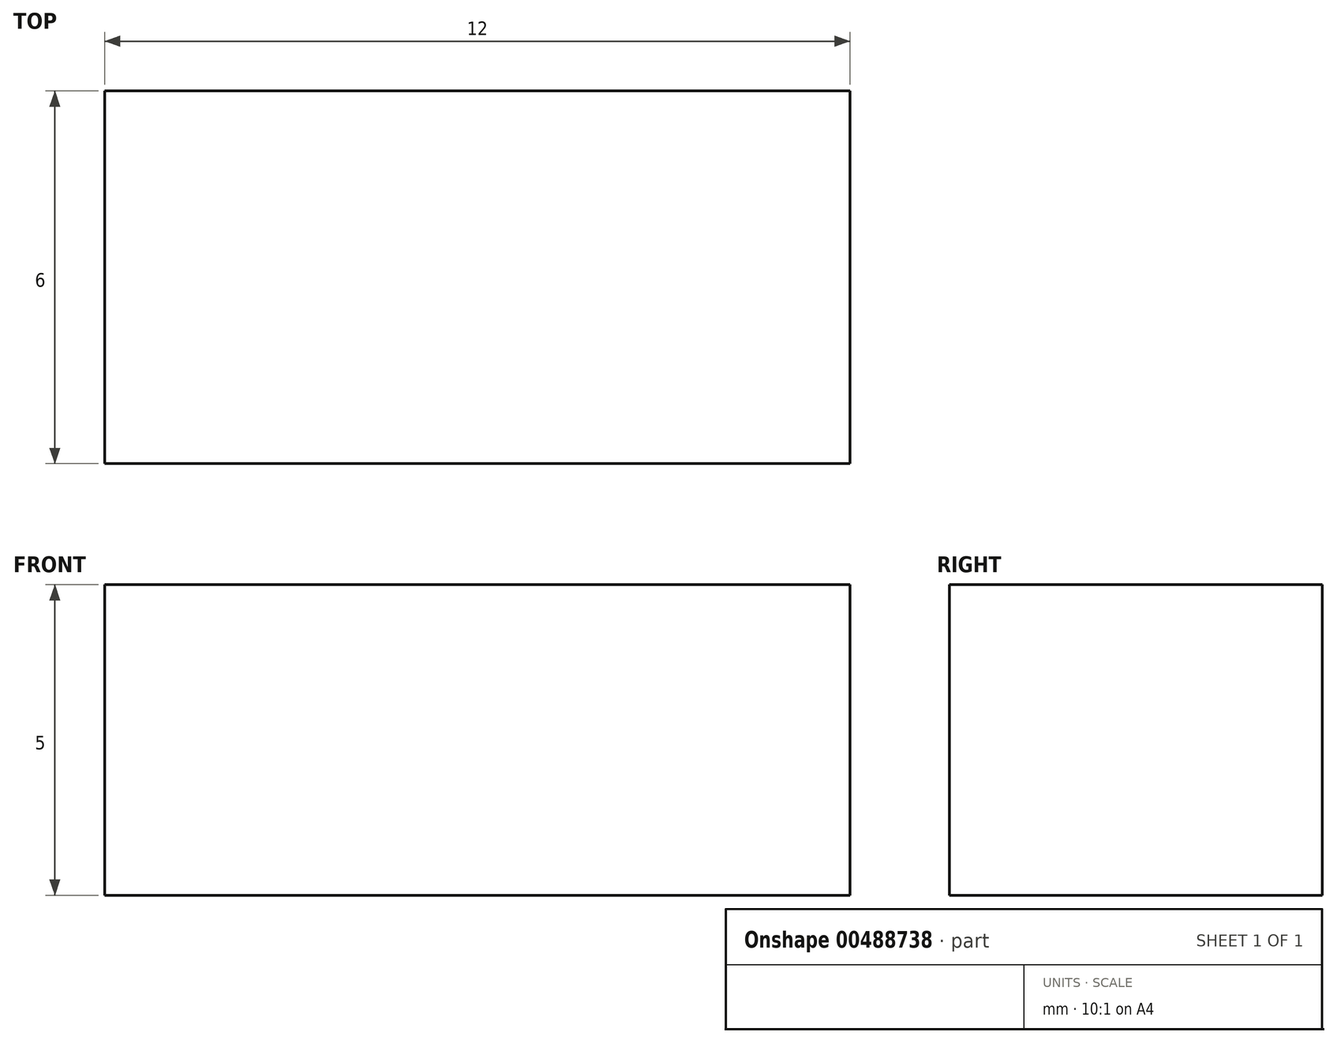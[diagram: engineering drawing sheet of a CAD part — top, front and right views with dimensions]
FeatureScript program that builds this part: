
annotation { "Feature Type Name" : "Feature", "Feature Type Description" : "" }
export const myFeature = defineFeature(function(context is Context, id is Id, definition is map)
    precondition{}
    {
        {
            var Q0;
            Q0=qCreatedBy(makeId("Top.planeOp"),FACE);
            var sketch = newSketch(context, id + "F0", { "sketchPlane" : qUnion([Q0])});
            skLineSegment(sketch, "E0.bottom", {"start": v(0, 0) * mm, "end": v(12, 0) * mm});
            skLineSegment(sketch, "E0.top", {"start": v(0, 6) * mm, "end": v(12, 6) * mm});
            skLineSegment(sketch, "E0.left", {"start": v(0, 0) * mm, "end": v(0, 6) * mm});
            skLineSegment(sketch, "E0.right", {"start": v(12, 0) * mm, "end": v(12, 6) * mm});
            skSolve(sketch);
        }
        {
            var Q0;
            Q0=makeQuery(id+"F0.imprint","IMPRINT",FACE,{"disambiguationData":[TD([[makeQuery(id+"F0.imprint","IMPRINT",EDGE,{"derivedFrom":sQuery(id+"F0.wireOp",EDGE,"E0.bottom")}),1.0]])]});
            extrude(context, id + "F1", {"entities" : qUnion([Q0]), "depth" : 5 * mm});
        }
    });
